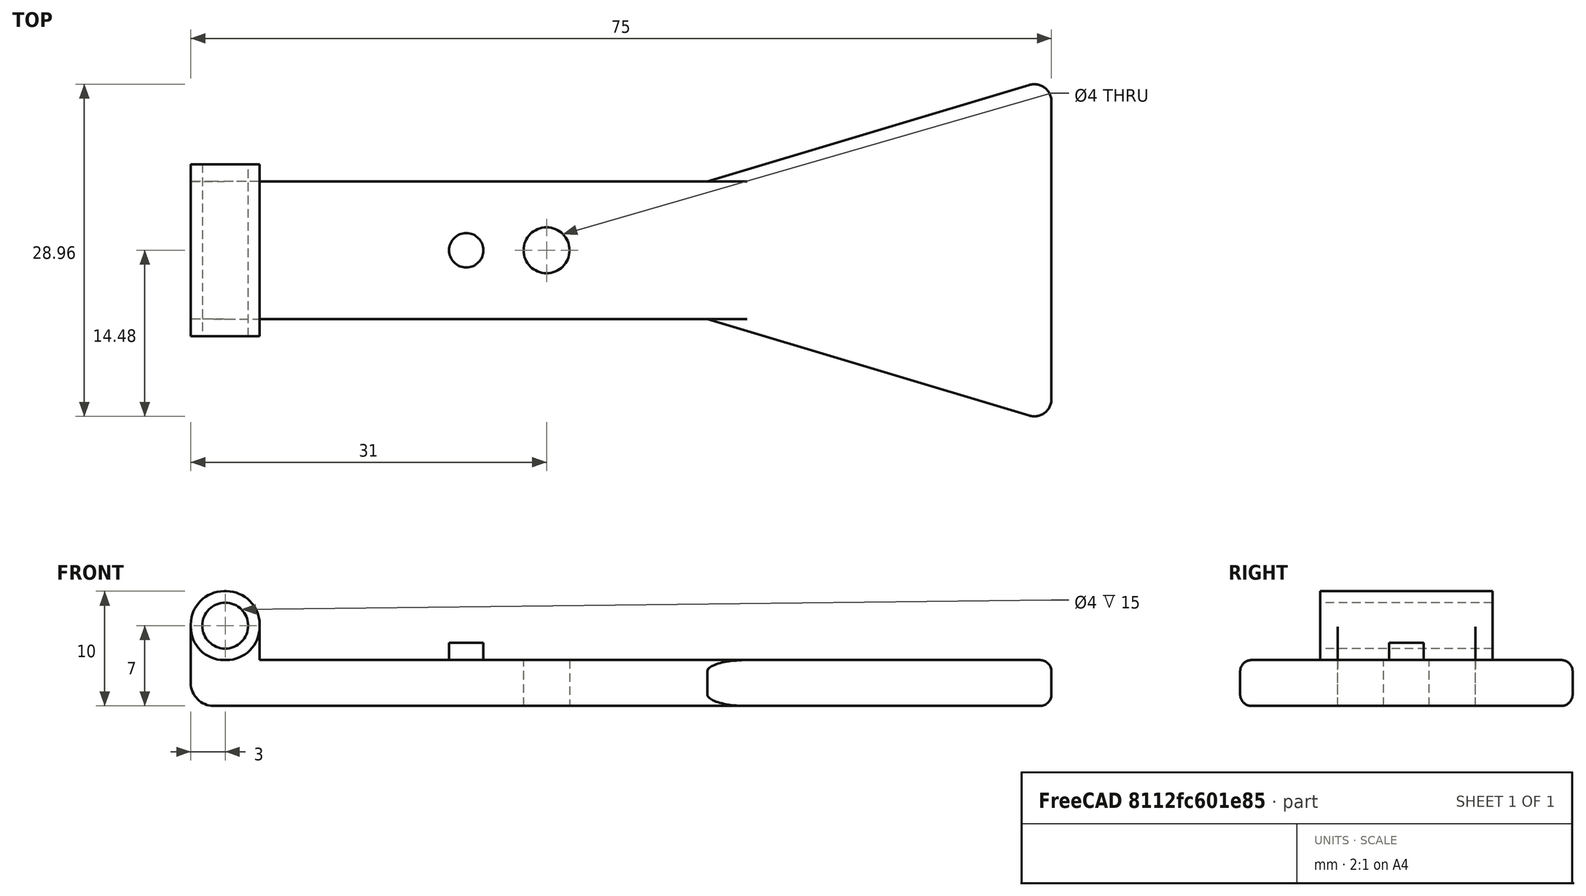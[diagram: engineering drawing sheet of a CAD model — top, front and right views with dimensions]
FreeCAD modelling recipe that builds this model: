
FCSTD DOCUMENT  (FreeCAD 1.0R39109 (Git))
Label: Key4_RD
License: All rights reserved
LicenseURL: http://en.wikipedia.org/wiki/All_rights_reserved
objects: Sketcher::SketchObject×5, PartDesign::Fillet×4, PartDesign::Pad×3, PartDesign::Pocket×2, Spreadsheet::Sheet×1, PartDesign::Body×1, App::Part×1
note: 38 computed .brp shape members not serialized (recipe doc carries the construction recipe); baked Part::Feature solids carry a one-line shape summary decoded from their .brp

FEATURE [Spreadsheet::Sheet] Spreadsheet  label="p"
  cells = A1='button_stem_diameter; B1(button_stem_diameter)=6; A2='button_stem_length; B2(button_stem_length)=8.15; A3='button_body_width; B3(button_body_width)=12; A4='button_body_length; B4(button_body_length)=12; A5='button_body_depth; B5(button_body_depth)=4.2; A6='button_lug_spacing; B6(button_lug_spacing)=4; A7='button_lug_diameter; B7(button_lug_diameter)=1.1; A9='key_stem_length; B9(key_stem_length)=45; A10='key_paddle_length; B10(key_paddle_length)=30; A11='key_paddle_width; B11(key_paddle_width)=30; A12='key_paddle_thickness; B12(key_paddle_thickness)=4; A14='key_lug_length; B14(key_lug_length)=3; A16='spring_wire_diameter; B16(spring_wire_diameter)=1.2; A18='box_outer_width; B18(box_outer_width)=53; A19='box_outer_length; B19(box_outer_length)=75; A20='box_outer_depth; B20(box_outer_depth)=32; A22='box_inner_width; B22(box_inner_width)==B18 - B29 * 2; C22='Calculated; A23='box_inner_length; B23(box_inner_length)==B19 - B29 * 2; C23='Calculated; A24='box_inner_depth; B24(box_inner_depth)==B20 - B29; C24='Calculated; A26='box_outer_radius; B26(box_outer_radius)==B29 + 2; C26='Calculated; A27='box_inner_radius; B27(box_inner_radius)==B26 / 2; C27='Calculated; A29='box_wall_thickness; B29(box_wall_thickness)=2; A30='box_wall_clearance; B30(box_wall_clearance)==B29 * 0.2; C30='Calculated 20%; A32='lug_insert_diameter; B32(lug_insert_diameter)=3.9; A33='lug_depth; B33(lug_depth)==B24 - B29; A34='lug_outer_radius; B34(lug_outer_radius)==B32 * 2.5; A36='face_fillet; B36(face_fillet)=1; A38='lid_ridge_size; B38(lid_ridge_size)=1.5; A39='lid_screw_diameter; B39(lid_screw_diameter)=3; A40='lid_screw_chamfer; B40(lid_screw_chamfer)=1.98; A42='button_lip_clearance; B42(button_lip_clearance)=2.75; A43='stand_length; B43(stand_length)=15.15
FEATURE [Sketcher::SketchObject] Sketch
  ArcFitTolerance = 0
  AttachmentSupport = -> [XY_Plane001]
  FullyConstrained = true
  MakeInternals = false
  MapMode = 5
  expr: Constraints[12] = <<p>>.button_body_length
  expr: Constraints[13] = <<p>>.button_body_length / 2
  expr: Constraints[14] = <<p>>.key_stem_length
  expr: Constraints[15] = <<p>>.key_paddle_length
  expr: Constraints[16] = <<p>>.key_paddle_length / 2
  expr: Constraints[17] = <<p>>.key_paddle_width
  sketch-geometry (6):
    g0: LineSegment StartX=0 StartY=6 StartZ=0 EndX=-45 EndY=6 EndZ=0
    g1: LineSegment StartX=-45 StartY=6 StartZ=0 EndX=-45 EndY=-6 EndZ=0
    g2: LineSegment StartX=-45 StartY=-6 StartZ=0 EndX=0 EndY=-6 EndZ=0
    g3: LineSegment StartX=0 StartY=-6 StartZ=0 EndX=30 EndY=-15 EndZ=0
    g4: LineSegment StartX=30 StartY=-15 StartZ=0 EndX=30 EndY=15 EndZ=0
    g5: LineSegment StartX=30 StartY=15 StartZ=0 EndX=0 EndY=6 EndZ=0
  constraints (18):
    c: PointOnObject(g0,g-2)
    c: Horizontal(g0)
    c: Coincident(g0,g1)
    c: Vertical(g1)
    c: Coincident(g1,g2)
    c: PointOnObject(g2,g-2)
    c: Horizontal(g2)
    c: Coincident(g2,g3)
    c: Coincident(g3,g4)
    c: Vertical(g4)
    c: Coincident(g4,g5)
    c: Coincident(g5,g0)
    c: DistanceY(g1,g1) = 12
    c: DistanceY(g-1,g0) = 6
    c: DistanceX(g0,g0) = 45
    c: DistanceY(g4,g4) = 30
    c: DistanceY(g-1,g4) = 15
    c: DistanceX(g-1,g4) = 30
FEATURE [PartDesign::Pad] Pad  label="KeyPad"
  Direction = (0,0,1)
  Length = 4
  Length2 = 10
  Profile = -> Sketch
  ReferenceAxis = -> Sketch [N_Axis]
  Suppressed = false
  Type = 0
  expr: Length = <<p>>.key_paddle_thickness
FEATURE [PartDesign::Fillet] Fillet  label="KeyEdgeFillet"
  Base = -> Pad [Edge14,Edge11]
  BaseFeature = -> Pad
  Radius = 1.5
  SupportTransform = false
  Suppressed = false
  UseAllEdges = false
FEATURE [PartDesign::Fillet] Fillet001  label="KeySoftEdgeFillet"
  Base = -> Fillet [Edge20,Edge11,Edge9,Edge18,Edge16,Edge7,Edge4,Edge1,Edge5,Edge13]
  BaseFeature = -> Fillet
  Radius = 1
  SupportTransform = false
  Suppressed = false
  UseAllEdges = false
FEATURE [Sketcher::SketchObject] Sketch003
  ArcFitTolerance = 0
  FullyConstrained = true
  MakeInternals = false
  MapMode = 5
  Placement = pos=(0,0,3.5) rot=(0,0,1;0rad)
  sketch-geometry (1):
    g0: Circle CenterX=-21 CenterY=0 CenterZ=0 NormalX=0 NormalY=0 NormalZ=1 AngleXU=0 Radius=1.5
  constraints (3):
    c: PointOnObject(g0,g-1)
    c: DistanceX(g0,g-1) = 21
    c: Diameter(g0) = 3
FEATURE [PartDesign::Pad] Pad003  label="KeyButtonMounts"
  BaseFeature = -> Fillet001
  Direction = (0,0,1)
  Length = 2
  Length2 = 10
  Profile = -> Sketch003
  ReferenceAxis = -> Sketch003 [N_Axis]
  Suppressed = false
  Type = 0
  expr: Length = 2
FEATURE [PartDesign::Fillet] Fillet002
  Base = -> Pad003 [Edge26]
  BaseFeature = -> Pad003
  Radius = 2
  SupportTransform = false
  Suppressed = false
  UseAllEdges = false
FEATURE [Sketcher::SketchObject] Sketch004
  ArcFitTolerance = 0
  AttachmentSupport = -> [Fillet002]
  FullyConstrained = true
  MakeInternals = false
  MapMode = 5
  Placement = pos=(0,0,4) rot=(0,0,1;0rad)
  expr: Constraints[10] = <<p>>.stand_length - 0.15
  expr: Constraints[11] = (<<p>>.stand_length - 0.15) / 2
  expr: Constraints[8] = <<p>>.key_stem_length
  sketch-geometry (4):
    g0: LineSegment StartX=-45 StartY=7.5 StartZ=0 EndX=-39 EndY=7.5 EndZ=0
    g1: LineSegment StartX=-39 StartY=7.5 StartZ=0 EndX=-39 EndY=-7.5 EndZ=0
    g2: LineSegment StartX=-39 StartY=-7.5 StartZ=0 EndX=-45 EndY=-7.5 EndZ=0
    g3: LineSegment StartX=-45 StartY=-7.5 StartZ=0 EndX=-45 EndY=7.5 EndZ=0
  constraints (12):
    c: Coincident(g0,g1)
    c: Coincident(g1,g2)
    c: Coincident(g2,g3)
    c: Coincident(g3,g0)
    c: Horizontal(g0)
    c: Horizontal(g2)
    c: Vertical(g1)
    c: Vertical(g3)
    c: DistanceX(g0,g-1) = 45
    c: DistanceX(g0,g0) = 6
    c: DistanceY(g1,g1) = 15
    c: DistanceY(g-1,g0) = 7.5
FEATURE [PartDesign::Pad] Pad004
  BaseFeature = -> Fillet002
  Direction = (0,0,1)
  Length = 6
  Length2 = 10
  Profile = -> Sketch004
  ReferenceAxis = -> Sketch004 [N_Axis]
  Suppressed = false
  Type = 0
FEATURE [Sketcher::SketchObject] Sketch005
  ArcFitTolerance = 0
  AttachmentSupport = -> [Pad004]
  FullyConstrained = true
  MakeInternals = false
  MapMode = 5
  Placement = pos=(0,-7.5,0) rot=(1,0,0;1.5708rad)
  expr: Constraints[1] = <<p>>.key_stem_length - 3
  expr: Constraints[2] = <<p>>.key_paddle_thickness + 3
  sketch-geometry (1):
    g0: Circle CenterX=-42 CenterY=7 CenterZ=0 NormalX=0 NormalY=0 NormalZ=1 AngleXU=0 Radius=2
  constraints (3):
    c: Diameter(g0) = 4
    c: DistanceX(g0,g-1) = 42
    c: DistanceY(g-1,g0) = 7
FEATURE [PartDesign::Pocket] Pocket
  BaseFeature = -> Pad004
  Direction = (0,1,-2e-16)
  Length = 5
  Length2 = 5
  Profile = -> Sketch005
  ReferenceAxis = -> Sketch005 [N_Axis]
  Suppressed = false
  Type = 1
FEATURE [PartDesign::Fillet] Fillet003
  Base = -> Pocket [Edge54,Edge58,Edge27,Edge25,Edge53,Edge57]
  BaseFeature = -> Pocket
  Radius = 2.9
  SupportTransform = false
  Suppressed = false
  UseAllEdges = false
FEATURE [Sketcher::SketchObject] Sketch006
  ArcFitTolerance = 0
  AttachmentSupport = -> [Fillet003]
  FullyConstrained = true
  MakeInternals = false
  MapMode = 5
  Placement = pos=(0,0,4) rot=(0,0,1;0rad)
  sketch-geometry (1):
    g0: Circle CenterX=-14 CenterY=0 CenterZ=0 NormalX=0 NormalY=0 NormalZ=1 AngleXU=0 Radius=2
  constraints (3):
    c: PointOnObject(g0,g-1)
    c: Diameter(g0) = 4
    c: DistanceX(g0,g-1) = 14
FEATURE [PartDesign::Pocket] Pocket001
  BaseFeature = -> Fillet003
  Direction = (0,0,-1)
  Length = 5
  Length2 = 5
  Profile = -> Sketch006
  ReferenceAxis = -> Sketch006 [N_Axis]
  Suppressed = false
  Type = 1
FEATURE [PartDesign::Body] Body  label="KeyBody"
  AllowCompound = false
  Group = -> [Sketch,Pad,Fillet,Fillet001,Sketch003,Pad003,Fillet002,Sketch004,Pad004,Sketch005,Pocket,Fillet003,Sketch006,Pocket001]
  Origin = -> Origin001
  Tip = -> Pocket001
FEATURE [App::Part] Part  label="KeyPart"
  Group = -> [Body]
  Origin = -> Origin
